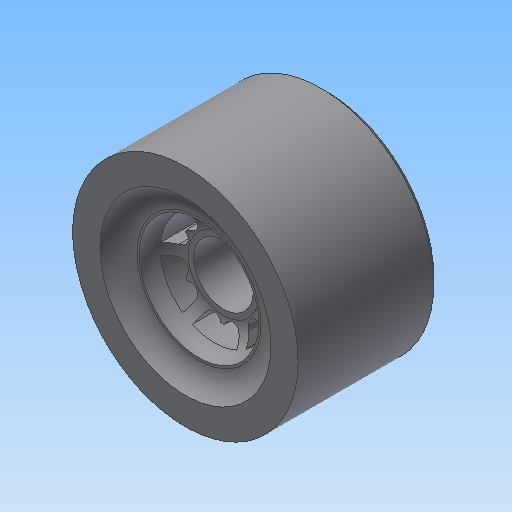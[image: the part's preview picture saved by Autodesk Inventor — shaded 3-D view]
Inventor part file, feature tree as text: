
AUTODESK INVENTOR PART (.ipt)
format: ipt  version: 2017 (Build 210142000, 142)  size: 318,976 bytes
history: native  units: in
note: dims shown in document units (in); Inventor stores cm internally (conversion verified against a paired STEP export)
features: extrude x4, fillet x4, sketch x1, other x1, chamfer x1
ambient origin geometry x8: Origin, YZ Plane, XZ Plane, XY Plane, X Axis, Y Axis, Z Axis, Center Point
bodies: Solid1 (feature_tree)
feature tree (11):
  sketch  "Sketch1"  dims[d0=3.2677in d1=0.3937in d2=0.315in d3=0.8661in d4=2.0472in d5=0.0in d6=1.6535in d7=0.0in d8=0.9449in d9=0.0in d10=0.3937in d11=1.7323in d14=60.0deg d15=2.3622in d17=360.0deg d19=0.3543in d20=0.8661in d21=0.0in d23=0.0787in d24=0.0787in d25=0.0787in d26=45.0deg d27=0.4331in d28=0.3543in]
  extrude  "Outside"  Depth=0.3937in
  extrude  "Middle"  Depth=0.3937in
  extrude  "Inside"  Depth=0.3937in
  fillet  "outside-outer fillet"  Radius=2.0472in
  other  "spokes"
  fillet  "outside-spoke fillet"  Radius=1.6535in
  chamfer  "inside-edge chamfer"  Distance=0.9449in
  fillet  "inside-outer fillet"  Radius=0.3937in
  fillet  "inside-spoke fillet"  Radius=1.7323in
  extrude  "spoke cutouts"  TaperAngle=60.0deg  [1 undecoded]
note: 1 required parameter value undecoded (feature->parameter linkage not recoverable at this tier; creation-order binding heuristic only, values carry confidence <= 0.55)
